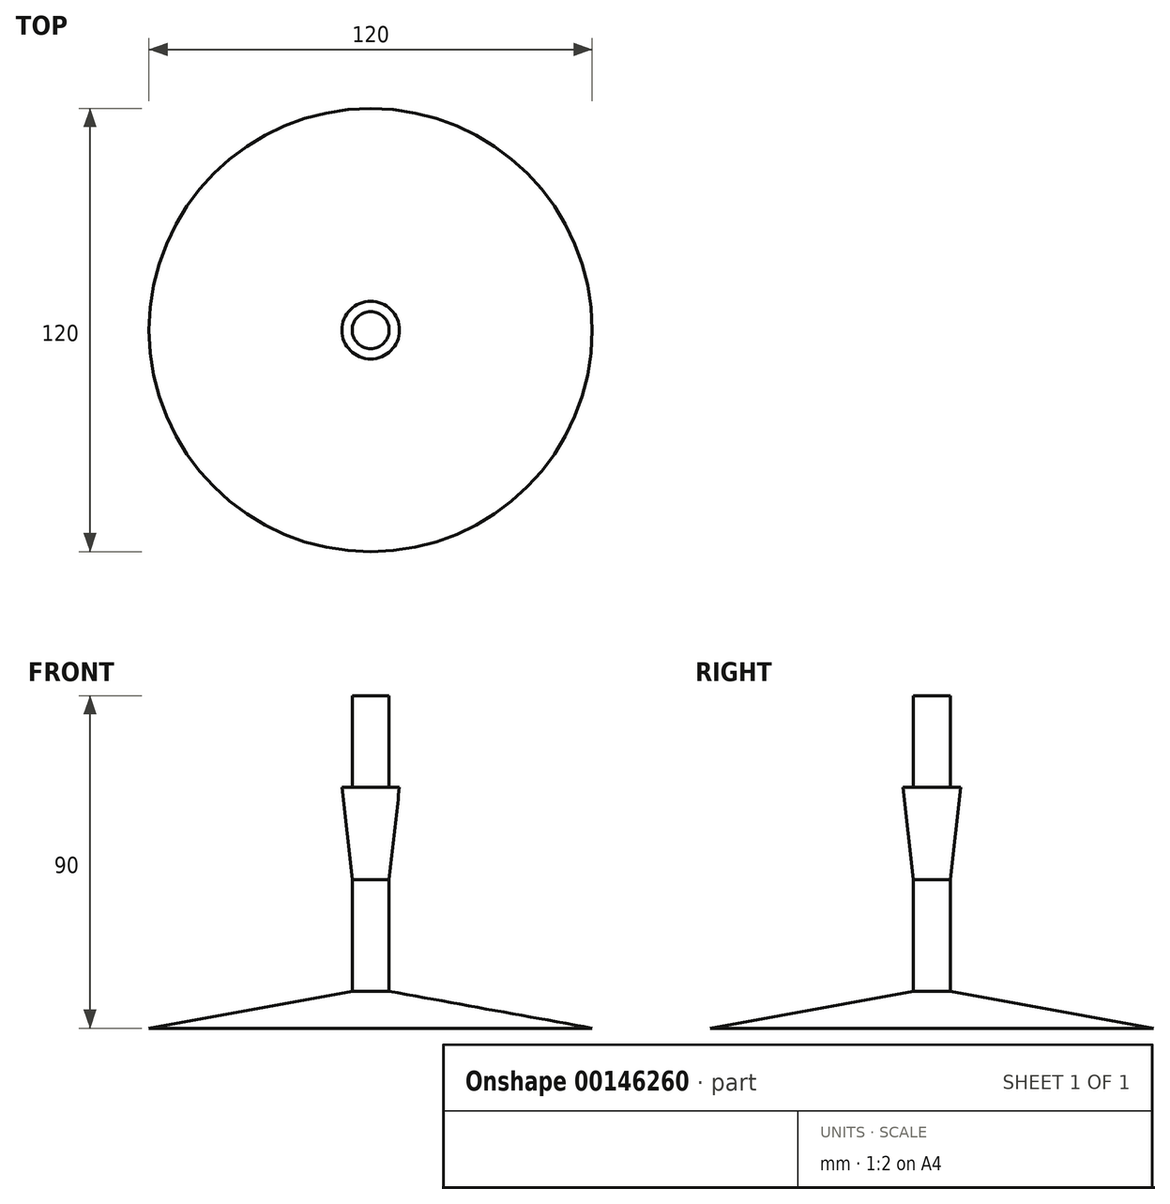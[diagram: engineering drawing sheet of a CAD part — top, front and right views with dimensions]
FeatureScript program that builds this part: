
annotation { "Feature Type Name" : "Feature", "Feature Type Description" : "" }
export const myFeature = defineFeature(function(context is Context, id is Id, definition is map)
    precondition{}
    {
        {
            var Q0;
            Q0=qCreatedBy(makeId("Top.planeOp"),FACE);
            var sketch = newSketch(context, id + "F0", { "sketchPlane" : qUnion([Q0])});
            skCircle(sketch, "E0", {"center": v(0, 0) * mm, "radius": 60 * mm});
            skSolve(sketch);
        }
        {
            var Q0;
            Q0=qCreatedBy(makeId("Top.planeOp"),FACE);
            cPlane(context, id + "F1", {"entities" : qUnion([Q0]), "cplaneType" : CPlaneType.OFFSET, "offset" : 10 * mm, "width" : 150 * mm, "height" : 150 * mm});
        }
        {
            var Q0;
            Q0=qCreatedBy(id+"F1.planeOp",FACE);
            var sketch = newSketch(context, id + "F2", { "sketchPlane" : qUnion([Q0])});
            skCircle(sketch, "E1", {"center": v(0, 0) * mm, "radius": 5 * mm});
            skSolve(sketch);
        }
        {
            var Q0;
            Q0 = qSketchRegion(id + "F2", true);
            extrude(context, id + "F3", {"entities" : qUnion([Q0]), "depth" : 80 * mm});
        }
        {
            var Q1;
            Q1=makeQuery(id+"F0.imprint","IMPRINT",FACE,{"disambiguationData":[TD([[makeQuery(id+"F0.imprint","IMPRINT",EDGE,{"derivedFrom":sQuery(id+"F0.wireOp",EDGE,"E0")}),1.0]])]});
            var Q2;
            Q2=makeQuery(id+"F3.opExtrude","CAP_FACE",FACE,{"disambiguationData":[OSD([sQuery(id+"F2.wireOp",EDGE,"E1")])],"isStart":true});
            loft(context, id + "F4", {"operationType" : NewBodyOperationType.ADD, "sheetProfilesArray" : [{ "sheetProfileEntities" : qUnion([Q1]) }, { "sheetProfileEntities" : qUnion([Q2]) }]});
        }
        {
            var Q0;
            Q0=makeQuery(id+"F3.opExtrude","CAP_FACE",FACE,{"disambiguationData":[OSD([sQuery(id+"F2.wireOp",EDGE,"E1")])],"isStart":false});
            cPlane(context, id + "F5", {"entities" : qUnion([Q0]), "cplaneType" : CPlaneType.OFFSET, "offset" : 24.75 * mm, "oppositeDirection" : true, "width" : 150 * mm, "height" : 150 * mm});
        }
        {
            var Q0;
            Q0=qCreatedBy(id+"F5.planeOp",FACE);
            var sketch = newSketch(context, id + "F6", { "sketchPlane" : qUnion([Q0])});
            skCircle(sketch, "E2", {"center": v(0, 0) * mm, "radius": 7.8 * mm});
            skSolve(sketch);
        }
        {
            var Q0;
            Q0=qCreatedBy(id+"F5.planeOp",FACE);
            cPlane(context, id + "F7", {"entities" : qUnion([Q0]), "cplaneType" : CPlaneType.OFFSET, "offset" : 25 * mm, "oppositeDirection" : true, "width" : 150 * mm, "height" : 150 * mm});
        }
        {
            var Q0;
            Q0=qCreatedBy(id+"F7.planeOp",FACE);
            var sketch = newSketch(context, id + "F8", { "sketchPlane" : qUnion([Q0])});
            skCircle(sketch, "E3", {"center": v(0, 0) * mm, "radius": 5 * mm});
            skSolve(sketch);
        }
        {
            var Q1;
            Q1 = qSketchRegion(id + "F8", true);
            var Q2;
            Q2 = qSketchRegion(id + "F6", true);
            loft(context, id + "F9", {"operationType" : NewBodyOperationType.ADD, "sheetProfilesArray" : [{ "sheetProfileEntities" : qUnion([Q1]) }, { "sheetProfileEntities" : qUnion([Q2]) }]});
        }
    });
